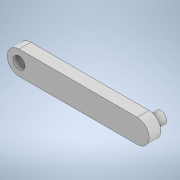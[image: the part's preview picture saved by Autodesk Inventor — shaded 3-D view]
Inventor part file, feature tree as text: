
AUTODESK INVENTOR PART (.ipt)
format: ipt  version: 2022 (Build 260153000, 153)  size: 108,032 bytes
history: native  units: mm
features: extrude x2, sketch x1
ambient origin geometry x8: Origin, YZ Plane, XZ Plane, XY Plane, X Axis, Y Axis, Z Axis, Center Point
bodies: Solid1 (feature_tree)
feature tree (3):
  sketch  "Sketch1"  dims[d0=50.0mm d1=10.0mm d2=5.0mm d3=5.0mm d4=0.0mm d5=5.0mm d6=0.0mm]
  extrude  "Extrusion1"  Depth=10.0mm
  extrude  "Extrusion2"  Depth=5.0mm
